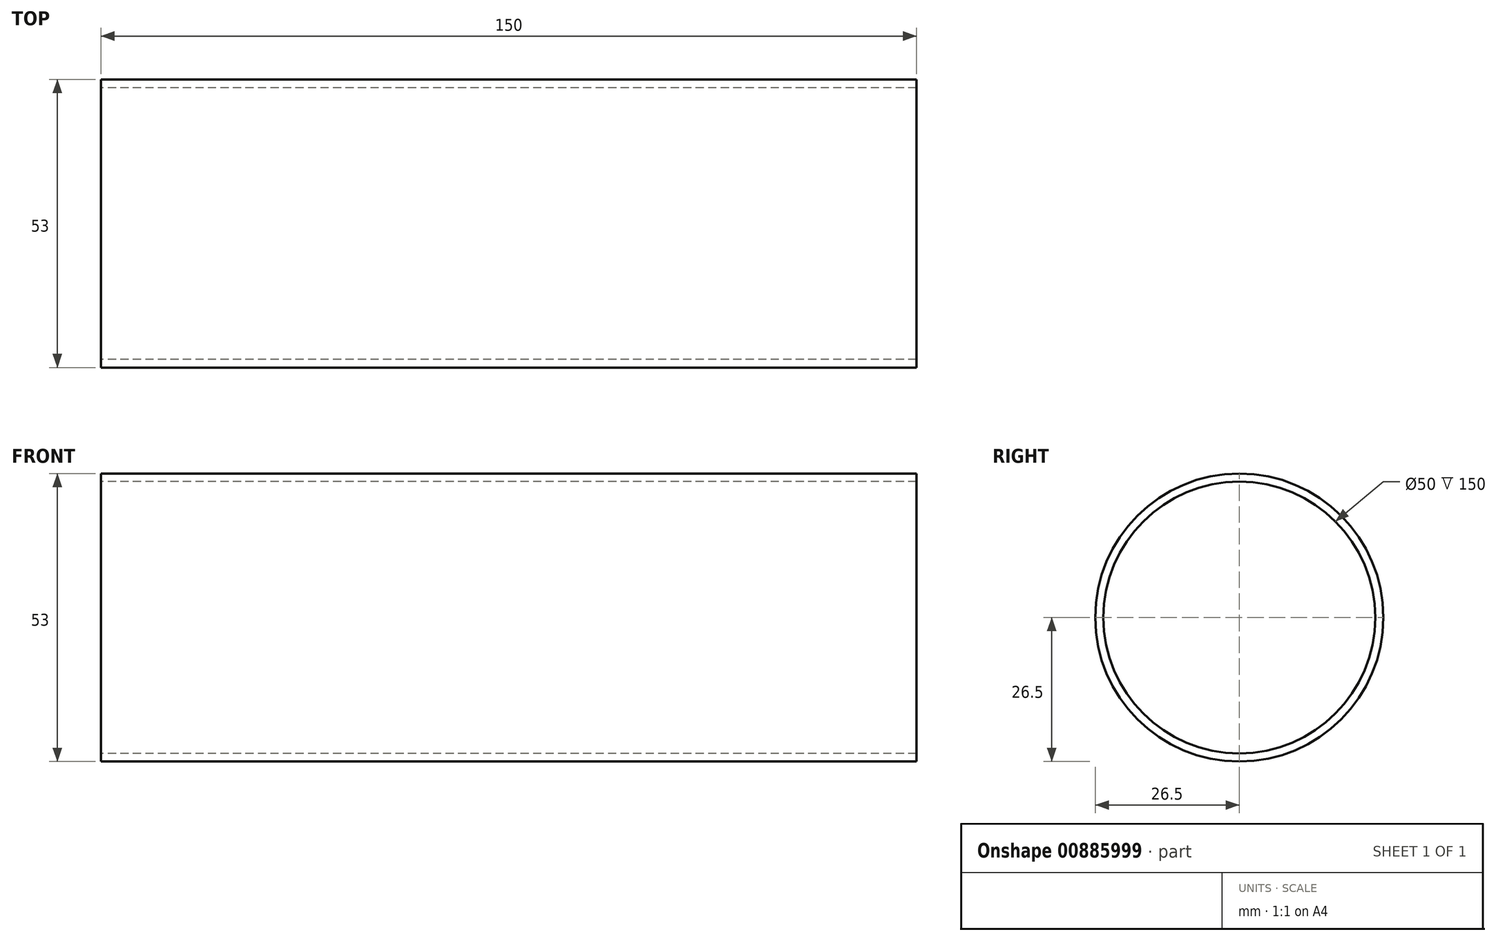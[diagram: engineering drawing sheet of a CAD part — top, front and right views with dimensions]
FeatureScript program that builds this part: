
annotation { "Feature Type Name" : "Feature", "Feature Type Description" : "" }
export const myFeature = defineFeature(function(context is Context, id is Id, definition is map)
    precondition{}
    {
        {
            var Q0;
            Q0=qCreatedBy(makeId("Right.planeOp"),FACE);
            var sketch = newSketch(context, id + "F0", { "sketchPlane" : qUnion([Q0])});
            skCircle(sketch, "E0", {"center": v(0, 0) * mm, "radius": 25 * mm});
            skCircle(sketch, "E1", {"center": v(0, 0) * mm, "radius": 26.5 * mm});
            skSolve(sketch);
        }
        {
            var Q0;
            Q0=makeQuery(id+"F0.imprint","IMPRINT",FACE,{"disambiguationData":[TD([[makeQuery(id+"F0.imprint","IMPRINT",EDGE,{"derivedFrom":sQuery(id+"F0.wireOp",EDGE,"E0")}),-1.0]])]});
            extrude(context, id + "F1", {"entities" : qUnion([Q0]), "depth" : 150 * mm, "offsetDistance" : 25 * mm});
        }
    });
